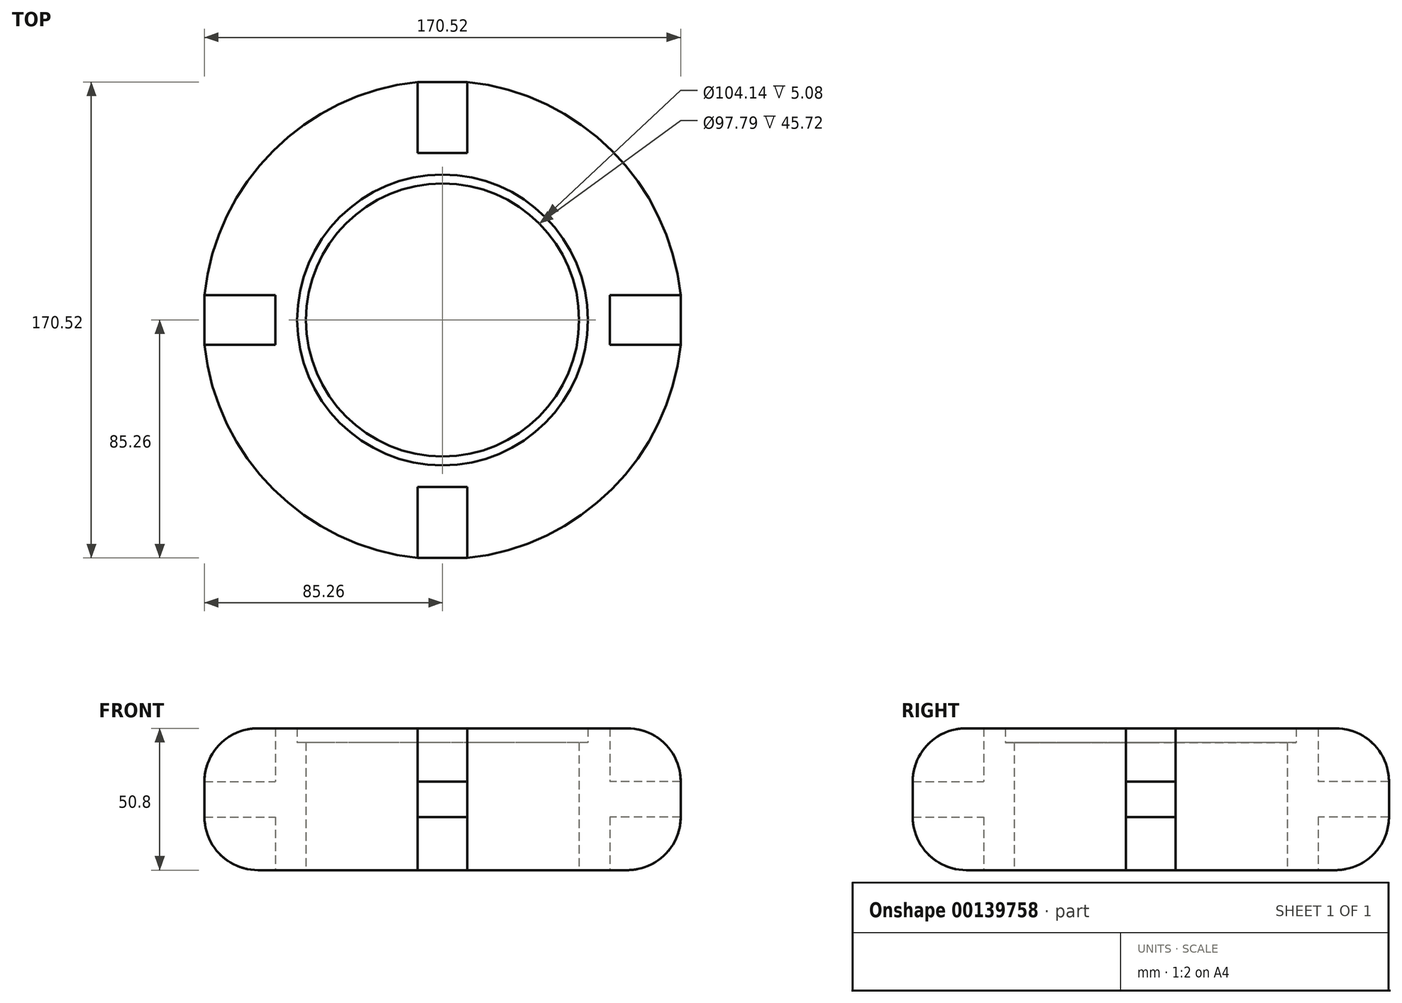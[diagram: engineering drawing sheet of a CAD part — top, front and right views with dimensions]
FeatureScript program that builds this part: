
annotation { "Feature Type Name" : "Feature", "Feature Type Description" : "" }
export const myFeature = defineFeature(function(context is Context, id is Id, definition is map)
    precondition{}
    {
        {
            var Q0;
            Q0=qCreatedBy(makeId("Top.planeOp"),FACE);
            var sketch = newSketch(context, id + "F0", { "sketchPlane" : qUnion([Q0])});
            skCircle(sketch, "E0", {"center": v(0, 0) * mm, "radius": 85.73 * mm});
            skLineSegment(sketch, "E1", {"start": v(-85.26, 8.9) * mm, "end": v(-59.86, 8.9) * mm});
            skLineSegment(sketch, "E2", {"start": v(-85.26, -8.9) * mm, "end": v(-59.86, -8.9) * mm});
            skLineSegment(sketch, "E3", {"start": v(-59.86, 8.89) * mm, "end": v(-59.86, -8.9) * mm});
            skLineSegment(sketch, "E4", {"start": v(85.26, 8.9) * mm, "end": v(59.86, 8.9) * mm});
            skLineSegment(sketch, "E5", {"start": v(85.26, -8.9) * mm, "end": v(59.86, -8.9) * mm});
            skLineSegment(sketch, "E6", {"start": v(59.86, 8.9) * mm, "end": v(59.86, -8.9) * mm});
            skLineSegment(sketch, "E7", {"start": v(-8.9, -85.26) * mm, "end": v(-8.9, -59.86) * mm});
            skLineSegment(sketch, "E8", {"start": v(8.9, -85.26) * mm, "end": v(8.9, -59.86) * mm});
            skLineSegment(sketch, "E9", {"start": v(-8.9, 85.26) * mm, "end": v(-8.9, 59.86) * mm});
            skLineSegment(sketch, "E10", {"start": v(8.9, 85.26) * mm, "end": v(8.9, 59.86) * mm});
            skLineSegment(sketch, "E11", {"start": v(-8.89, -59.86) * mm, "end": v(8.9, -59.86) * mm});
            skLineSegment(sketch, "E12", {"start": v(-8.89, 59.86) * mm, "end": v(8.9, 59.86) * mm});
            skCircle(sketch, "E13", {"center": v(0, 0) * mm, "radius": 52.07 * mm});
            skCircle(sketch, "E14", {"center": v(0, 0) * mm, "radius": 48.9 * mm});
            skSolve(sketch);
        }
        {
            var Q0;
            {var subQ3=sQuery(id+"F0.wireOp",EDGE,"E1");Q0=makeQuery(id+"F0.imprint","IMPRINT",FACE,{"disambiguationData":[TD([[makeQuery(id+"F0.imprint","IMPRINT",EDGE,{"derivedFrom":subQ3}),1.0]])]});}
            extrude(context, id + "F1", {"entities" : qUnion([Q0]), "depth" : 50.8 * mm});
        }
        {
            var Q0;
            {var subQ0=sQuery(id+"F0.wireOp",EDGE,"E0");Q0=makeQuery(id+"F1.opExtrude","CAP_EDGE",EDGE,{"disambiguationData":[OSD([subQ0]),TDD([makeQuery(id+"F0.imprint","IMPRINT",EDGE,{"disambiguationData":[TD([[makeQuery(id+"F0.imprint","INTERSECT",VERTEX,{"derivedFrom":[subQ0,sQuery(id+"F0.wireOp",EDGE,"E2")]}),-1.0]])],"derivedFrom":subQ0})])],"isStart":false});}
            var Q1;
            {var subQ0=sQuery(id+"F0.wireOp",EDGE,"E0");Q1=makeQuery(id+"F1.opExtrude","CAP_EDGE",EDGE,{"disambiguationData":[OSD([subQ0]),TDD([makeQuery(id+"F0.imprint","IMPRINT",EDGE,{"disambiguationData":[TD([[makeQuery(id+"F0.imprint","INTERSECT",VERTEX,{"derivedFrom":[subQ0,sQuery(id+"F0.wireOp",EDGE,"E5")]}),1.0]])],"derivedFrom":subQ0})])],"isStart":false});}
            var Q2;
            {var subQ0=sQuery(id+"F0.wireOp",EDGE,"E0");Q2=makeQuery(id+"F1.opExtrude","CAP_EDGE",EDGE,{"disambiguationData":[OSD([subQ0]),TDD([makeQuery(id+"F0.imprint","IMPRINT",EDGE,{"disambiguationData":[TD([[makeQuery(id+"F0.imprint","INTERSECT",VERTEX,{"derivedFrom":[subQ0,sQuery(id+"F0.wireOp",EDGE,"E4")]}),-1.0]])],"derivedFrom":subQ0})])],"isStart":false});}
            var Q3;
            {var subQ0=sQuery(id+"F0.wireOp",EDGE,"E0");Q3=makeQuery(id+"F1.opExtrude","CAP_EDGE",EDGE,{"disambiguationData":[OSD([subQ0]),TDD([makeQuery(id+"F0.imprint","IMPRINT",EDGE,{"disambiguationData":[TD([[makeQuery(id+"F0.imprint","INTERSECT",VERTEX,{"derivedFrom":[subQ0,sQuery(id+"F0.wireOp",EDGE,"E1")]}),1.0]])],"derivedFrom":subQ0})])],"isStart":false});}
            var Q4;
            {var subQ0=sQuery(id+"F0.wireOp",EDGE,"E0");Q4=makeQuery(id+"F1.opExtrude","CAP_EDGE",EDGE,{"disambiguationData":[OSD([subQ0]),TDD([makeQuery(id+"F0.imprint","IMPRINT",EDGE,{"disambiguationData":[TD([[makeQuery(id+"F0.imprint","INTERSECT",VERTEX,{"derivedFrom":[subQ0,sQuery(id+"F0.wireOp",EDGE,"E5")]}),1.0]])],"derivedFrom":subQ0})])],"isStart":true});}
            var Q5;
            {var subQ0=sQuery(id+"F0.wireOp",EDGE,"E0");Q5=makeQuery(id+"F1.opExtrude","CAP_EDGE",EDGE,{"disambiguationData":[OSD([subQ0]),TDD([makeQuery(id+"F0.imprint","IMPRINT",EDGE,{"disambiguationData":[TD([[makeQuery(id+"F0.imprint","INTERSECT",VERTEX,{"derivedFrom":[subQ0,sQuery(id+"F0.wireOp",EDGE,"E4")]}),-1.0]])],"derivedFrom":subQ0})])],"isStart":true});}
            var Q6;
            {var subQ0=sQuery(id+"F0.wireOp",EDGE,"E0");Q6=makeQuery(id+"F1.opExtrude","CAP_EDGE",EDGE,{"disambiguationData":[OSD([subQ0]),TDD([makeQuery(id+"F0.imprint","IMPRINT",EDGE,{"disambiguationData":[TD([[makeQuery(id+"F0.imprint","INTERSECT",VERTEX,{"derivedFrom":[subQ0,sQuery(id+"F0.wireOp",EDGE,"E2")]}),-1.0]])],"derivedFrom":subQ0})])],"isStart":true});}
            var Q7;
            {var subQ0=sQuery(id+"F0.wireOp",EDGE,"E0");Q7=makeQuery(id+"F1.opExtrude","CAP_EDGE",EDGE,{"disambiguationData":[OSD([subQ0]),TDD([makeQuery(id+"F0.imprint","IMPRINT",EDGE,{"disambiguationData":[TD([[makeQuery(id+"F0.imprint","INTERSECT",VERTEX,{"derivedFrom":[subQ0,sQuery(id+"F0.wireOp",EDGE,"E1")]}),1.0]])],"derivedFrom":subQ0})])],"isStart":true});}
            fillet(context, id + "F2", {"entities" : qUnion([Q0, Q1, Q2, Q3, Q4, Q5, Q6, Q7]), "radius" : 19.05 * mm, "tangentPropagation" : true, "allowEdgeOverflow" : false});
        }
        {
            var Q0;
            Q0=makeQuery(id+"F1.opExtrude","SWEPT_FACE",FACE,{"disambiguationData":[OSD([sQuery(id+"F0.wireOp",EDGE,"E7")])]});
            var sketch = newSketch(context, id + "F3", { "sketchPlane" : qUnion([Q0])});
            skLineSegment(sketch, "E15", {"start": v(-85.26, 31.75) * mm, "end": v(-59.86, 31.75) * mm});
            skLineSegment(sketch, "E16", {"start": v(-85.26, 19.05) * mm, "end": v(-59.86, 19.05) * mm});
            skSolve(sketch);
        }
        {
            var Q0;
            Q0=makeQuery(id+"F1.opExtrude","SWEPT_FACE",FACE,{"disambiguationData":[OSD([sQuery(id+"F0.wireOp",EDGE,"E1")])]});
            var sketch = newSketch(context, id + "F4", { "sketchPlane" : qUnion([Q0])});
            skLineSegment(sketch, "E17", {"start": v(-85.26, 31.75) * mm, "end": v(-59.86, 31.75) * mm});
            skLineSegment(sketch, "E18", {"start": v(-85.26, 19.05) * mm, "end": v(-59.86, 19.05) * mm});
            skSolve(sketch);
        }
        {
            var Q0;
            Q0=makeQuery(id+"F1.opExtrude","SWEPT_FACE",FACE,{"disambiguationData":[OSD([sQuery(id+"F0.wireOp",EDGE,"E5")])]});
            var sketch = newSketch(context, id + "F5", { "sketchPlane" : qUnion([Q0])});
            skLineSegment(sketch, "E19", {"start": v(-85.26, 31.75) * mm, "end": v(-59.86, 31.75) * mm});
            skLineSegment(sketch, "E20", {"start": v(-85.26, 19.05) * mm, "end": v(-59.86, 19.05) * mm});
            skSolve(sketch);
        }
        {
            var Q0;
            Q0=makeQuery(id+"F1.opExtrude","SWEPT_FACE",FACE,{"disambiguationData":[OSD([sQuery(id+"F0.wireOp",EDGE,"E10")])]});
            var sketch = newSketch(context, id + "F6", { "sketchPlane" : qUnion([Q0])});
            skLineSegment(sketch, "E21", {"start": v(-85.26, 31.75) * mm, "end": v(-59.86, 31.75) * mm});
            skLineSegment(sketch, "E22", {"start": v(-85.26, 19.05) * mm, "end": v(-59.86, 19.05) * mm});
            skSolve(sketch);
        }
        {
            var Q0;
            {var subQ0=sQuery(id+"F5.wireOp",EDGE,"E19");Q0=makeQuery(id+"F5.imprint","IMPRINT",FACE,{"disambiguationData":[TD([[makeQuery(id+"F5.imprint","IMPRINT",EDGE,{"derivedFrom":subQ0}),-1.0]])]});}
            extrude(context, id + "F7", {"entities" : qUnion([Q0]), "operationType" : NewBodyOperationType.ADD, "depth" : 17.78 * mm});
        }
        {
            var Q0;
            {var subQ0=sQuery(id+"F6.wireOp",EDGE,"E21");Q0=makeQuery(id+"F6.imprint","IMPRINT",FACE,{"disambiguationData":[TD([[makeQuery(id+"F6.imprint","IMPRINT",EDGE,{"derivedFrom":subQ0}),-1.0]])]});}
            extrude(context, id + "F8", {"entities" : qUnion([Q0]), "operationType" : NewBodyOperationType.ADD, "depth" : 17.78 * mm});
        }
        {
            var Q0;
            {var subQ0=sQuery(id+"F4.wireOp",EDGE,"E17");Q0=makeQuery(id+"F4.imprint","IMPRINT",FACE,{"disambiguationData":[TD([[makeQuery(id+"F4.imprint","IMPRINT",EDGE,{"derivedFrom":subQ0}),-1.0]])]});}
            extrude(context, id + "F9", {"entities" : qUnion([Q0]), "operationType" : NewBodyOperationType.ADD, "depth" : 17.78 * mm});
        }
        {
            var Q0;
            {var subQ0=sQuery(id+"F3.wireOp",EDGE,"E15");Q0=makeQuery(id+"F3.imprint","IMPRINT",FACE,{"disambiguationData":[TD([[makeQuery(id+"F3.imprint","IMPRINT",EDGE,{"derivedFrom":subQ0}),-1.0]])]});}
            extrude(context, id + "F10", {"entities" : qUnion([Q0]), "operationType" : NewBodyOperationType.ADD, "depth" : 17.78 * mm});
        }
        {
            var Q0;
            Q0=makeQuery(id+"F0.imprint","IMPRINT",FACE,{"disambiguationData":[TD([[makeQuery(id+"F0.imprint","IMPRINT",EDGE,{"derivedFrom":sQuery(id+"F0.wireOp",EDGE,"E13")}),1.0]])]});
            extrude(context, id + "F11", {"entities" : qUnion([Q0]), "operationType" : NewBodyOperationType.ADD, "depth" : 45.72 * mm});
        }
    });
